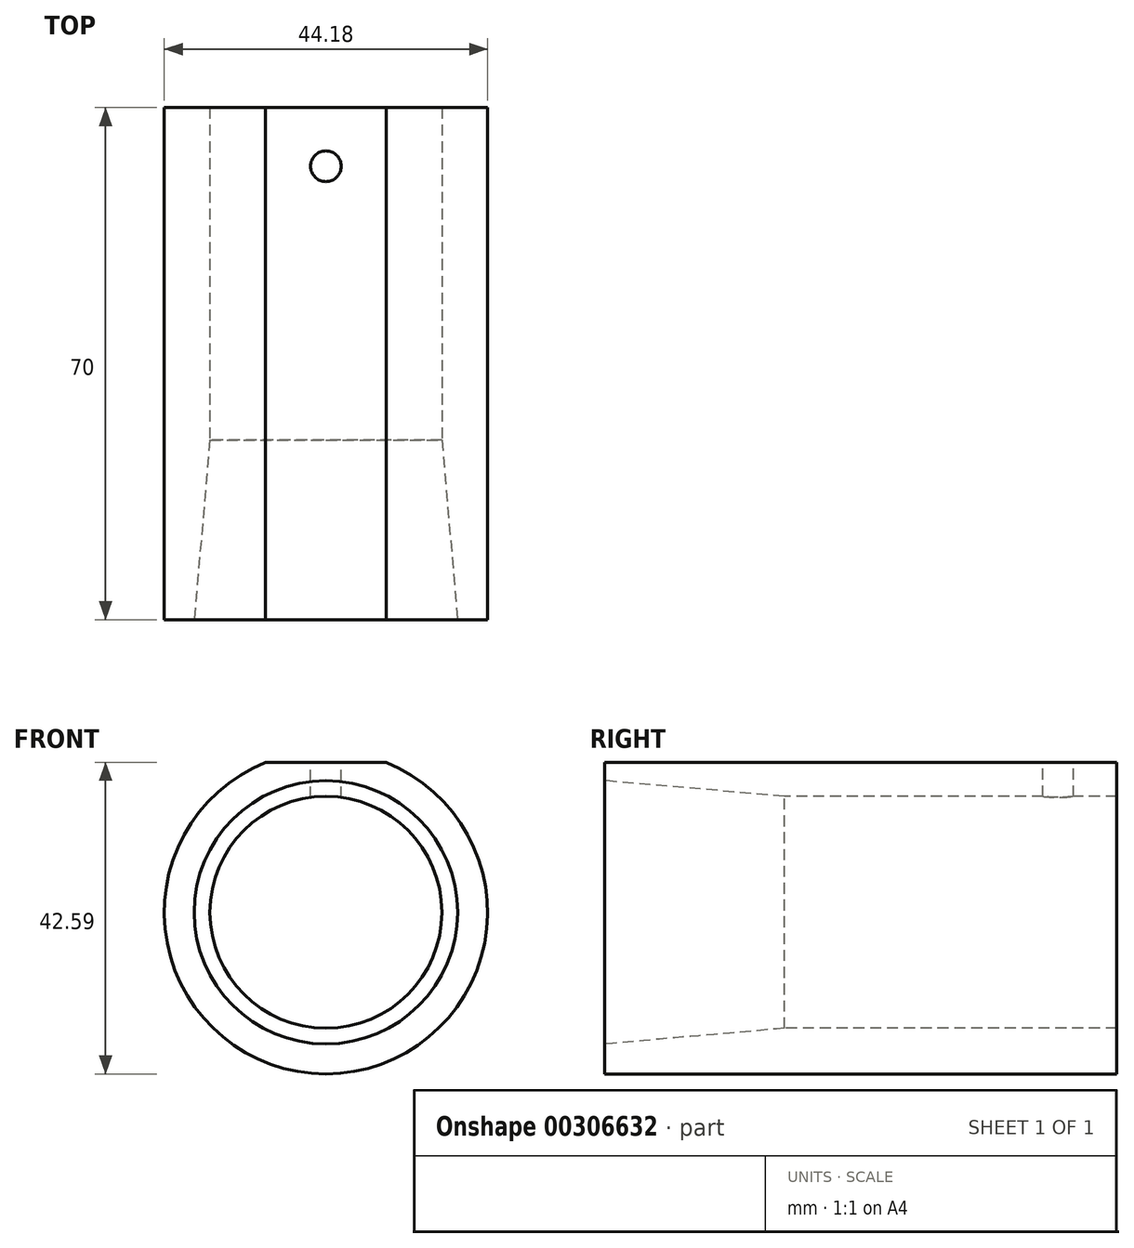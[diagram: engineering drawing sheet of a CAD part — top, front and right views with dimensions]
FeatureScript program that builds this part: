
annotation { "Feature Type Name" : "Feature", "Feature Type Description" : "" }
export const myFeature = defineFeature(function(context is Context, id is Id, definition is map)
    precondition{}
    {
        {
            var Q0;
            Q0=qCreatedBy(makeId("Front.planeOp"),FACE);
            var sketch = newSketch(context, id + "F0", { "sketchPlane" : qUnion([Q0])});
            skCircle(sketch, "E0", {"center": v(0, 0) * mm, "radius": 22.1 * mm});
            skCircle(sketch, "E1", {"center": v(0, 0) * mm, "radius": 15.85 * mm});
            skSolve(sketch);
        }
        {
            var Q0;
            Q0=qSketchRegion(id+"F0",true);
            extrude(context, id + "F1", {"entities" : qUnion([Q0]), "oppositeDirection" : true, "depth" : 70 * mm});
        }
        {
            var Q0;
            Q0=makeQuery(id+"F1.opExtrude","CAP_FACE",FACE,{"disambiguationData":[OSD([sQuery(id+"F0.wireOp",EDGE,"E0"),sQuery(id+"F0.wireOp",EDGE,"E1")])],"isStart":true});
            var sketch = newSketch(context, id + "F2", { "sketchPlane" : qUnion([Q0])});
            skCircle(sketch, "E2", {"center": v(0, 0) * mm, "radius": 18 * mm});
            skSolve(sketch);
        }
        {
            var Q0;
            Q0=qSketchRegion(id+"F2",true);
            extrude(context, id + "F3", {"entities" : qUnion([Q0]), "operationType" : NewBodyOperationType.REMOVE, "oppositeDirection" : true, "depth" : 25 * mm, "hasDraft" : true, "draftAngle" : 5 * degree, "draftPullDirection" : true});
        }
        {
            var Q0;
            Q0=makeQuery(id+"F1.opExtrude","CAP_FACE",FACE,{"disambiguationData":[OSD([sQuery(id+"F0.wireOp",EDGE,"E0"),sQuery(id+"F0.wireOp",EDGE,"E1")])],"isStart":true});
            var sketch = newSketch(context, id + "F4", { "sketchPlane" : qUnion([Q0])});
            skLineSegment(sketch, "E3", {"start": v(-8.23, 20.5) * mm, "end": v(8.23, 20.5) * mm});
            skArc(sketch, "E4", {"start": v(8.23, 20.5) * mm, "mid": v(0, 22.09) * mm, "end": v(-8.23, 20.5) * mm});
            skSolve(sketch);
        }
        {
            var Q0;
            Q0=qSketchRegion(id+"F4",true);
            extrude(context, id + "F5", {"entities" : qUnion([Q0]), "operationType" : NewBodyOperationType.REMOVE, "endBound" : BoundingType.THROUGH_ALL, "oppositeDirection" : true, "depth" : 25 * mm});
        }
        {
            var Q0;
            Q0=makeQuery(id+"F5.boolean.opBoolean","COPY",FACE,{"derivedFrom":makeQuery(id+"F5.opExtrude","SWEPT_FACE",FACE,{"disambiguationData":[OSD([sQuery(id+"F4.wireOp",EDGE,"E3")])]})});
            var sketch = newSketch(context, id + "F6", { "sketchPlane" : qUnion([Q0])});
            skPoint(sketch, "E5", {"position": v(0, 62) * mm});
            skSolve(sketch);
        }
        {
            var Q0;
            Q0=sQuery(id+"F6.wireOp",VERTEX,"E5");
            var Q1;
            Q1=makeQuery(id+"F1.opExtrude","SWEPT_BODY",BODY,{"disambiguationData":[OSD([sQuery(id+"F0.wireOp",EDGE,"E0"),sQuery(id+"F0.wireOp",EDGE,"E1")])]});
            hole(context, id + "F7", {"style" : HoleStyle.SIMPLE, "endStyle" : HoleEndStyle.BLIND, "standardTappedOrClearance" : lookupTablePath({ "standard" : "ISO", "engagement" : "75%", "pitch" : "0.8 mm", "size" : "M5", "type" : "Tapped" }), "standardBlindInLast" : lookupTablePath({ "standard" : "ISO", "engagement" : "75%", "pitch" : "0.8 mm", "size" : "M5", "type" : "Tapped" }), "holeDiameter" : 4.2 * mm, "showTappedDepth" : true, "holeDepth" : 7.6 * mm, "tappedDepth" : 6 * mm, "tapClearance" : 2, "locations" : qUnion([Q0]), "scope" : qUnion([Q1]), "majorDiameter" : 5 * mm});
        }
    });
